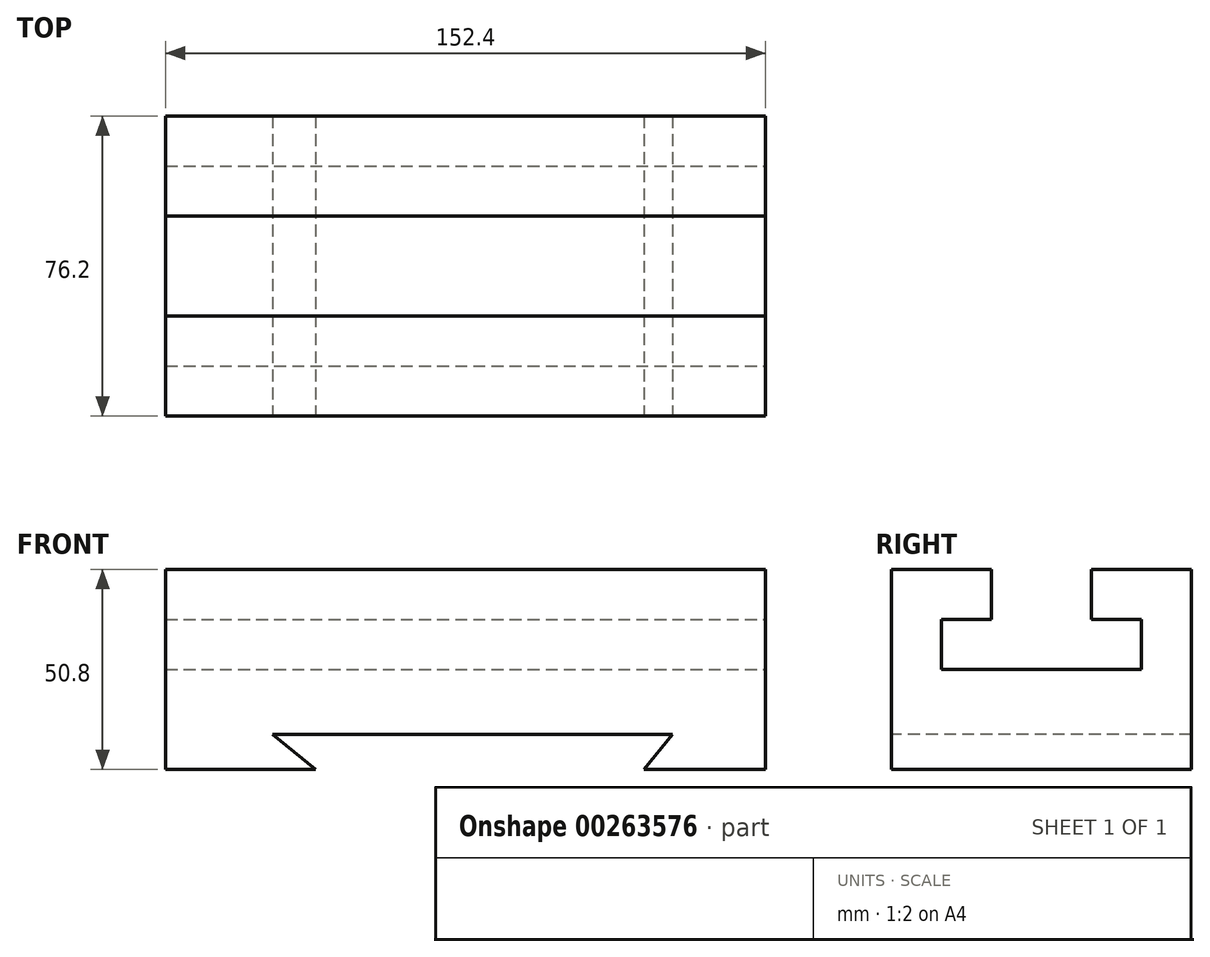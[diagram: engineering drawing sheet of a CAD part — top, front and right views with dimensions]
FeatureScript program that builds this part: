
annotation { "Feature Type Name" : "Feature", "Feature Type Description" : "" }
export const myFeature = defineFeature(function(context is Context, id is Id, definition is map)
    precondition{}
    {
        {
            var Q0;
            Q0=qCreatedBy(makeId("Front.planeOp"),FACE);
            var sketch = newSketch(context, id + "F0", { "sketchPlane" : qUnion([Q0])});
            skLineSegment(sketch, "E0.bottom", {"start": v(-68.07, 28.93) * mm, "end": v(84.33, 28.93) * mm});
            skLineSegment(sketch, "E0.top", {"start": v(-68.07, -21.87) * mm, "end": v(84.33, -21.87) * mm});
            skLineSegment(sketch, "E0.left", {"start": v(-68.07, 28.93) * mm, "end": v(-68.07, -21.87) * mm});
            skLineSegment(sketch, "E0.right", {"start": v(84.33, 28.93) * mm, "end": v(84.33, -21.87) * mm});
            skSolve(sketch);
        }
        {
            var Q0;
            Q0 = qSketchRegion(id + "F0", true);
            extrude(context, id + "F1", {"entities" : qUnion([Q0]), "depth" : 76.2 * mm});
        }
        {
            var Q0;
            Q0=makeQuery(id+"F1.opExtrude","CAP_FACE",FACE,{"disambiguationData":[OSD([sQuery(id+"F0.wireOp",EDGE,"E0.bottom"),sQuery(id+"F0.wireOp",EDGE,"E0.top"),sQuery(id+"F0.wireOp",EDGE,"E0.left"),sQuery(id+"F0.wireOp",EDGE,"E0.right")])],"isStart":false});
            var sketch = newSketch(context, id + "F2", { "sketchPlane" : qUnion([Q0])});
            skLineSegment(sketch, "E1", {"start": v(-29.97, -21.87) * mm, "end": v(-40.83, -12.95) * mm});
            skLineSegment(sketch, "E2", {"start": v(-40.83, -12.95) * mm, "end": v(60.77, -12.95) * mm});
            skLineSegment(sketch, "E3", {"start": v(60.77, -12.95) * mm, "end": v(53.44, -21.87) * mm});
            skLineSegment(sketch, "E4", {"start": v(-29.97, -21.87) * mm, "end": v(53.44, -21.87) * mm});
            skSolve(sketch);
        }
        {
            var Q0;
            Q0 = qSketchRegion(id + "F2", true);
            extrude(context, id + "F3", {"entities" : qUnion([Q0]), "operationType" : NewBodyOperationType.REMOVE, "endBound" : BoundingType.THROUGH_ALL, "oppositeDirection" : true, "depth" : 25.4 * mm});
        }
        {
            var Q0;
            Q0=makeQuery(id+"F1.opExtrude","SWEPT_FACE",FACE,{"disambiguationData":[OSD([sQuery(id+"F0.wireOp",EDGE,"E0.right")])]});
            var sketch = newSketch(context, id + "F4", { "sketchPlane" : qUnion([Q0])});
            skLineSegment(sketch, "E5", {"start": v(-50.8, 28.93) * mm, "end": v(-25.4, 28.93) * mm});
            skLineSegment(sketch, "E6", {"start": v(-25.4, 28.93) * mm, "end": v(-25.4, 16.23) * mm});
            skLineSegment(sketch, "E7", {"start": v(-25.4, 16.23) * mm, "end": v(-12.7, 16.23) * mm});
            skLineSegment(sketch, "E8", {"start": v(-12.7, 16.23) * mm, "end": v(-12.7, 3.53) * mm});
            skLineSegment(sketch, "E9", {"start": v(-12.7, 3.53) * mm, "end": v(-63.5, 3.53) * mm});
            skLineSegment(sketch, "E10", {"start": v(-63.5, 3.53) * mm, "end": v(-63.5, 16.23) * mm});
            skLineSegment(sketch, "E11", {"start": v(-63.5, 16.23) * mm, "end": v(-50.8, 16.23) * mm});
            skLineSegment(sketch, "E12", {"start": v(-50.8, 16.23) * mm, "end": v(-50.8, 28.93) * mm});
            skSolve(sketch);
        }
        {
            var Q0;
            Q0=makeQuery(id+"F4.imprint","IMPRINT",FACE,{"disambiguationData":[TD([[makeQuery(id+"F4.imprint","IMPRINT",EDGE,{"derivedFrom":sQuery(id+"F4.wireOp",EDGE,"E5")}),-1.0]])]});
            extrude(context, id + "F5", {"entities" : qUnion([Q0]), "operationType" : NewBodyOperationType.REMOVE, "endBound" : BoundingType.THROUGH_ALL, "oppositeDirection" : true, "depth" : 25.4 * mm});
        }
    });
